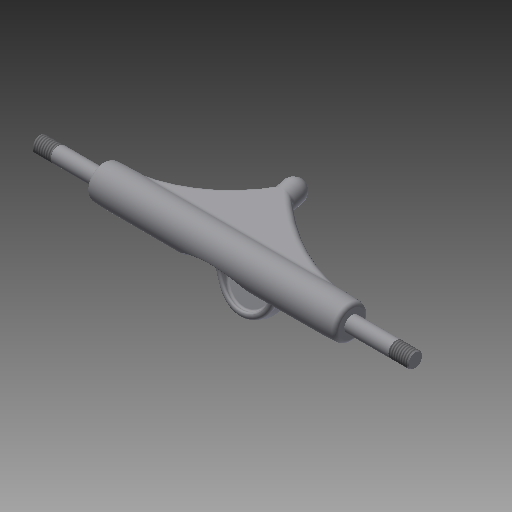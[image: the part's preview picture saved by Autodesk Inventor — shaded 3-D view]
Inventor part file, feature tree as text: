
AUTODESK INVENTOR PART (.ipt)
format: ipt  version: 2019 (Build 230136000, 136)  size: 1,440,768 bytes
history: native  units: mm
features: fillet x17, other x16, extrude x8, sketch x4, chamfer x2, loft x2, thread x1, mirror x1, revolve x1
ambient origin geometry x8: Origin, YZ Plane, XZ Plane, XY Plane, X Axis, Y Axis, Z Axis, Center Point
bodies: Solido1 (feature_tree)
feature tree (52):
  other  "Piano di lavoro10"
  extrude  "Estrusione10"  Depth=11.0mm
  other  "Asse di lavoro2"
  other  "Piano di lavoro14"
  extrude  "Estrusione11"  Depth=36.0mm TaperAngle=0.0deg
  other  "Piano di lavoro19"
  extrude  "Estrusione12"  Depth=130.0mm
  fillet  "Raccordo10"  Radius=29.0mm
  fillet  "Raccordo11"  Radius=5.5mm
  fillet  "Raccordo12"  [1 undecoded]
  chamfer  "Smusso3"  Distance=18.0mm
  fillet  "Raccordo13"  Radius=130.0mm
  extrude  "Estrusione15"  Depth=2.75mm
  thread  "Filettatura3"
  chamfer  "Smusso4"  Distance=2.0mm
  mirror  "Specchio6"
  other  "Piano di lavoro35"
  extrude  "Estrusione20"  Depth=3.0mm
  extrude  "Estrusione21"  Depth=8.0mm
  extrude  "Estrusione22"  Depth=2.0mm
  fillet  "Raccordo14"  Radius=8.0mm
  fillet  "Raccordo15"  Radius=33.0mm
  other  "Piano di lavoro39"
  sketch  "Schizzo66"
  other  "Asse di lavoro13"
  other  "Piano di lavoro40"
  loft  "Loft14"
  extrude  "Estrusione25"  Depth=0.5mm TaperAngle=45.0deg
  fillet  "Raccordo21"  Radius=24.0mm
  fillet  "Raccordo22"  Radius=3.0mm
  fillet  "Raccordo28"  Radius=30.0mm
  fillet  "Raccordo29"  Radius=5.0mm
  loft  "Loft16"
  revolve  "Rivoluzione3"
  fillet  "Raccordo31"  Radius=1.0mm
  fillet  "Raccordo34"  Radius=1.0mm
  fillet  "Raccordo35"  [1 undecoded]
  fillet  "Raccordo36"  [1 undecoded]
  fillet  "Raccordo37"  [1 undecoded]
  fillet  "Raccordo38"  Radius=2.0mm
  fillet  "Raccordo39"  Radius=2.0mm
  other  "Linea chiusa proiettata8"
  other  "Linea chiusa proiettata10"
  sketch  "Schizzo57"
  other  "Linea chiusa proiettata21"
  other  "Spigoli5"
  sketch  "Schizzo72"
  other  "Linea chiusa proiettata24"
  other  "Spigoli6"
  sketch  "Schizzo74"
  other  "Proietta spigoli di taglio11"
  other  "Proietta spigoli di taglio13"
note: 4 required parameter values undecoded (feature->parameter linkage not recoverable at this tier; creation-order binding heuristic only, values carry confidence <= 0.55)
